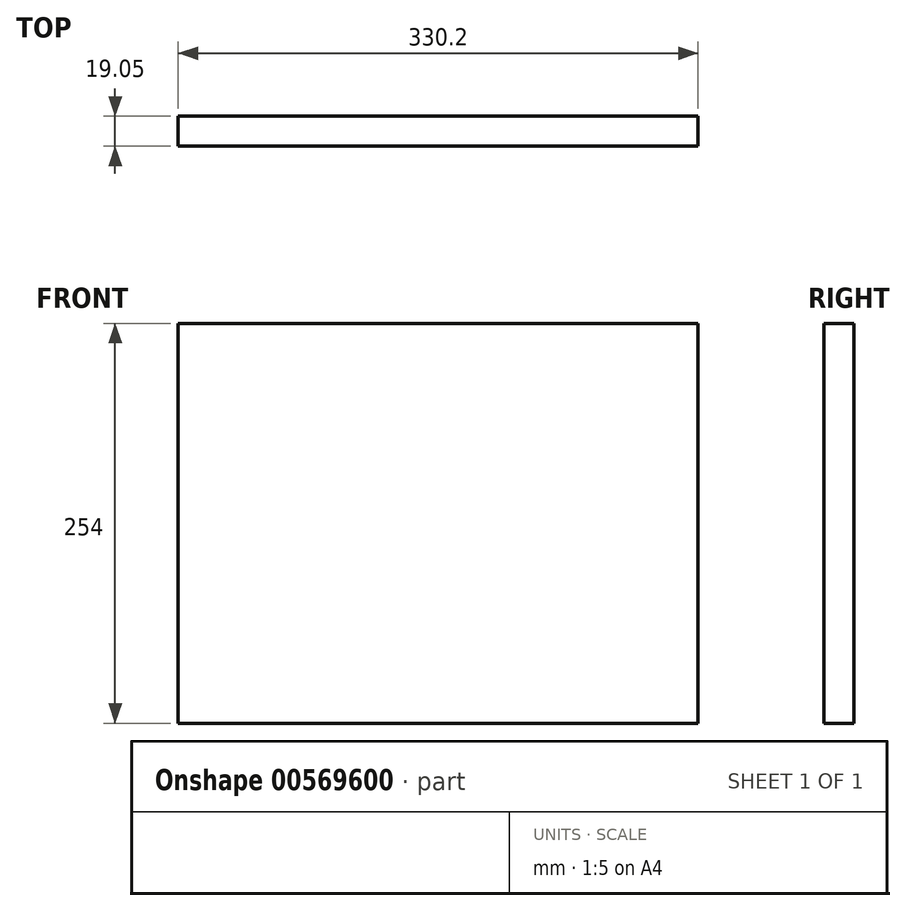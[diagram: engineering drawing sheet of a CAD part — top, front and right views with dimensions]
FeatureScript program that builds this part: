
annotation { "Feature Type Name" : "Feature", "Feature Type Description" : "" }
export const myFeature = defineFeature(function(context is Context, id is Id, definition is map)
    precondition{}
    {
        {
            var Q0;
            Q0=qCreatedBy(makeId("Front.planeOp"),FACE);
            var sketch = newSketch(context, id + "F0", { "sketchPlane" : qUnion([Q0])});
            skLineSegment(sketch, "E0.bottom", {"start": v(165.1, -127) * mm, "end": v(-165.1, -127) * mm});
            skLineSegment(sketch, "E0.top", {"start": v(165.1, 127) * mm, "end": v(-165.1, 127) * mm});
            skLineSegment(sketch, "E0.left", {"start": v(165.1, -127) * mm, "end": v(165.1, 127) * mm});
            skLineSegment(sketch, "E0.right", {"start": v(-165.1, -127) * mm, "end": v(-165.1, 127) * mm});
            skPoint(sketch, "E0.middle", {"position": v(0, 0) * mm});
            skSolve(sketch);
        }
        {
            var Q0;
            Q0 = qSketchRegion(id + "F0", true);
            extrude(context, id + "F1", {"entities" : qUnion([Q0]), "depth" : 19.05 * mm, "offsetDistance" : 25.4 * mm});
        }
    });
